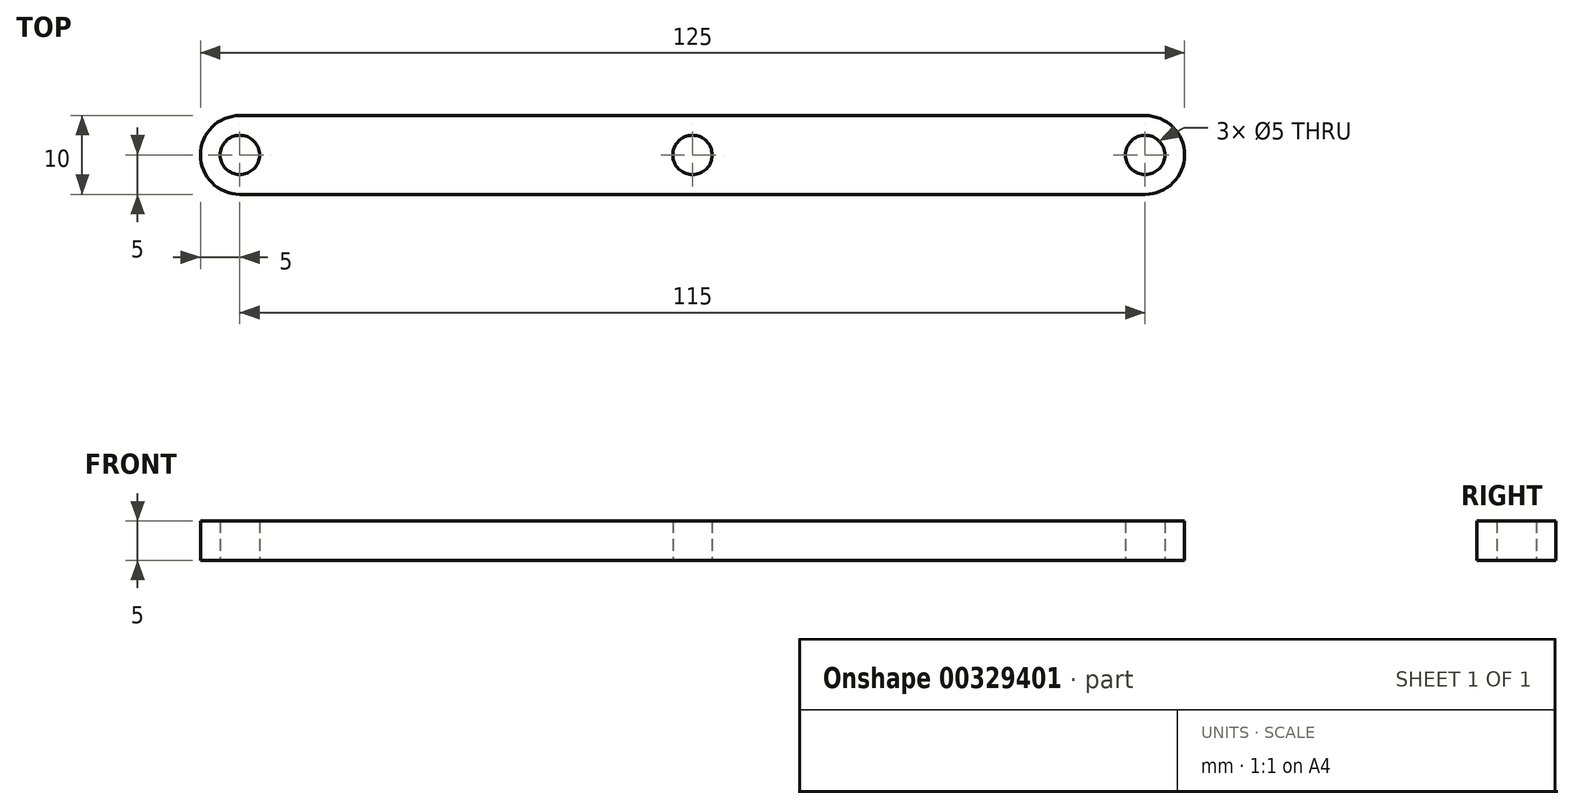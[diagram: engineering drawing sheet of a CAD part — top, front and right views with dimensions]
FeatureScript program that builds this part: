
annotation { "Feature Type Name" : "Feature", "Feature Type Description" : "" }
export const myFeature = defineFeature(function(context is Context, id is Id, definition is map)
    precondition{}
    {
        {
            var Q0;
            Q0=qCreatedBy(makeId("Top.planeOp"),FACE);
            var sketch = newSketch(context, id + "F0", { "sketchPlane" : qUnion([Q0])});
            skLineSegment(sketch, "E0.bottom", {"start": v(57.5, -5) * mm, "end": v(-57.5, -5) * mm});
            skLineSegment(sketch, "E0.top", {"start": v(57.5, 5) * mm, "end": v(-57.5, 5) * mm});
            skLineSegment(sketch, "E0.left", {"start": v(57.5, -5) * mm, "end": v(57.5, 5) * mm});
            skLineSegment(sketch, "E0.right", {"start": v(-57.5, -5) * mm, "end": v(-57.5, 5) * mm});
            skPoint(sketch, "E0.middle", {"position": v(0, 0) * mm});
            skCircle(sketch, "E1", {"center": v(-57.5, 0) * mm, "radius": 5 * mm});
            skCircle(sketch, "E2", {"center": v(57.5, 0) * mm, "radius": 5 * mm});
            skCircle(sketch, "E3", {"center": v(-57.5, 0) * mm, "radius": 2.5 * mm});
            skCircle(sketch, "E4", {"center": v(57.5, 0) * mm, "radius": 2.5 * mm});
            skCircle(sketch, "E5", {"center": v(0, 0) * mm, "radius": 2.5 * mm});
            skSolve(sketch);
        }
        {
            var Q0;
            {var subQ2=sQuery(id+"F0.wireOp",EDGE,"E0.bottom");Q0=makeQuery(id+"F0.imprint","IMPRINT",FACE,{"disambiguationData":[TD([[makeQuery(id+"F0.imprint","IMPRINT",EDGE,{"derivedFrom":subQ2}),-1.0]])]});}
            var Q1;
            {var subQ1=sQuery(id+"F0.wireOp",EDGE,"E0.right");var subQ3=sQuery(id+"F0.wireOp",EDGE,"E3");var subQ4=makeQuery(id+"F0.imprint","INTERSECT",VERTEX,{"disambiguationData":[OD(0.0)],"derivedFrom":[subQ1,subQ3]});Q1=makeQuery(id+"F0.imprint","IMPRINT",FACE,{"disambiguationData":[TD([[makeQuery(id+"F0.imprint","IMPRINT",EDGE,{"disambiguationData":[TD([[subQ4,-1.0]])],"derivedFrom":subQ3}),-1.0]])]});}
            var Q2;
            {var subQ1=sQuery(id+"F0.wireOp",EDGE,"E0.left");var subQ3=sQuery(id+"F0.wireOp",EDGE,"E4");var subQ4=makeQuery(id+"F0.imprint","INTERSECT",VERTEX,{"disambiguationData":[OD(0.0)],"derivedFrom":[subQ1,subQ3]});Q2=makeQuery(id+"F0.imprint","IMPRINT",FACE,{"disambiguationData":[TD([[makeQuery(id+"F0.imprint","IMPRINT",EDGE,{"disambiguationData":[TD([[subQ4,-1.0]])],"derivedFrom":subQ3}),-1.0]])]});}
            var Q3;
            {var subQ1=sQuery(id+"F0.wireOp",EDGE,"E0.left");var subQ3=sQuery(id+"F0.wireOp",EDGE,"E4");var subQ4=makeQuery(id+"F0.imprint","INTERSECT",VERTEX,{"disambiguationData":[OD(0.0)],"derivedFrom":[subQ1,subQ3]});Q3=makeQuery(id+"F0.imprint","IMPRINT",FACE,{"disambiguationData":[TD([[makeQuery(id+"F0.imprint","IMPRINT",EDGE,{"disambiguationData":[TD([[subQ4,1.0]])],"derivedFrom":subQ3}),-1.0]])]});}
            var Q4;
            {var subQ1=sQuery(id+"F0.wireOp",EDGE,"E0.right");var subQ3=sQuery(id+"F0.wireOp",EDGE,"E3");var subQ4=makeQuery(id+"F0.imprint","INTERSECT",VERTEX,{"disambiguationData":[OD(0.0)],"derivedFrom":[subQ1,subQ3]});Q4=makeQuery(id+"F0.imprint","IMPRINT",FACE,{"disambiguationData":[TD([[makeQuery(id+"F0.imprint","IMPRINT",EDGE,{"disambiguationData":[TD([[subQ4,1.0]])],"derivedFrom":subQ3}),-1.0]])]});}
            extrude(context, id + "F1", {"entities" : qUnion([Q0, Q1, Q2, Q3, Q4]), "depth" : 5 * mm});
        }
    });
